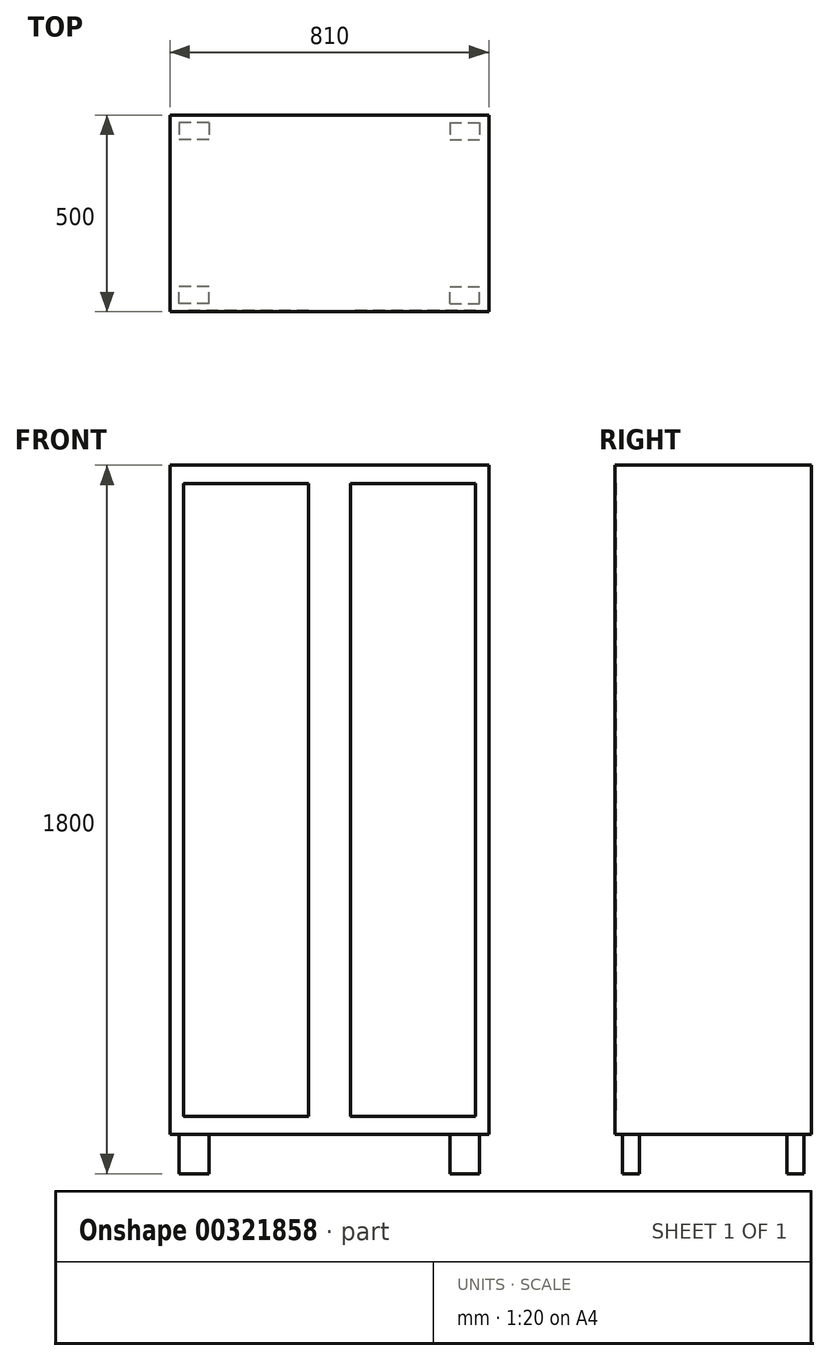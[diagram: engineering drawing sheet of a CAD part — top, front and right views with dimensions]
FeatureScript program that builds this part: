
annotation { "Feature Type Name" : "Feature", "Feature Type Description" : "" }
export const myFeature = defineFeature(function(context is Context, id is Id, definition is map)
    precondition{}
    {
        {
            var Q0;
            Q0=qCreatedBy(makeId("Top.planeOp"),FACE);
            var sketch = newSketch(context, id + "F0", { "sketchPlane" : qUnion([Q0])});
            skLineSegment(sketch, "E0.bottom", {"start": v(405, 250) * mm, "end": v(-405, 250) * mm});
            skLineSegment(sketch, "E0.top", {"start": v(405, -250) * mm, "end": v(-405, -250) * mm});
            skLineSegment(sketch, "E0.left", {"start": v(405, 250) * mm, "end": v(405, -250) * mm});
            skLineSegment(sketch, "E0.right", {"start": v(-405, 250) * mm, "end": v(-405, -250) * mm});
            skPoint(sketch, "E0.middle", {"position": v(0, 0) * mm});
            skSolve(sketch);
        }
        {
            var Q0;
            Q0=makeQuery(id+"F0.imprint","IMPRINT",FACE,{"disambiguationData":[TD([[makeQuery(id+"F0.imprint","IMPRINT",EDGE,{"derivedFrom":sQuery(id+"F0.wireOp",EDGE,"E0.bottom")}),1.0]])]});
            extrude(context, id + "F1", {"entities" : qUnion([Q0]), "depth" : 1700 * mm});
        }
        {
            var Q0;
            Q0=makeQuery(id+"F1.opExtrude","CAP_FACE",FACE,{"disambiguationData":[OSD([sQuery(id+"F0.wireOp",EDGE,"E0.bottom"),sQuery(id+"F0.wireOp",EDGE,"E0.top"),sQuery(id+"F0.wireOp",EDGE,"E0.left"),sQuery(id+"F0.wireOp",EDGE,"E0.right")])],"isStart":true});
            var sketch = newSketch(context, id + "F2", { "sketchPlane" : qUnion([Q0])});
            skLineSegment(sketch, "E1", {"start": v(-405, 0) * mm, "end": v(405, 0) * mm, "construction": true});
            skLineSegment(sketch, "E2", {"start": v(0, -250) * mm, "end": v(0, 250) * mm, "construction": true});
            skLineSegment(sketch, "E3.bottom", {"start": v(-306.12, 229.96) * mm, "end": v(-381.85, 229.96) * mm});
            skLineSegment(sketch, "E3.top", {"start": v(-306.12, 186.8) * mm, "end": v(-381.85, 186.8) * mm});
            skLineSegment(sketch, "E3.left", {"start": v(-306.12, 229.96) * mm, "end": v(-306.12, 186.8) * mm});
            skLineSegment(sketch, "E3.right", {"start": v(-381.85, 229.96) * mm, "end": v(-381.85, 186.8) * mm});
            skPoint(sketch, "E3.middle", {"position": v(-343.99, 208.38) * mm});
            skLineSegment(sketch, "E4.MirrorCS", {"start": v(381.85, 229.96) * mm, "end": v(381.85, 186.8) * mm});
            skLineSegment(sketch, "E5.MirrorCS", {"start": v(306.12, 229.96) * mm, "end": v(381.85, 229.96) * mm});
            skLineSegment(sketch, "E6.MirrorCS", {"start": v(306.12, 229.96) * mm, "end": v(306.12, 186.8) * mm});
            skLineSegment(sketch, "E7.MirrorCS", {"start": v(306.12, 186.8) * mm, "end": v(381.85, 186.8) * mm});
            skLineSegment(sketch, "E8.MirrorCS", {"start": v(381.85, -229.96) * mm, "end": v(381.85, -186.8) * mm});
            skLineSegment(sketch, "E9.MirrorCS", {"start": v(-381.85, -229.96) * mm, "end": v(-381.85, -186.8) * mm});
            skLineSegment(sketch, "E10.MirrorCS", {"start": v(-306.12, -229.96) * mm, "end": v(-306.12, -186.8) * mm});
            skLineSegment(sketch, "E11.MirrorCS", {"start": v(306.12, -229.96) * mm, "end": v(306.12, -186.8) * mm});
            skLineSegment(sketch, "E12.MirrorCS", {"start": v(-306.12, -186.8) * mm, "end": v(-381.85, -186.8) * mm});
            skLineSegment(sketch, "E13.MirrorCS", {"start": v(-306.12, -229.96) * mm, "end": v(-381.85, -229.96) * mm});
            skLineSegment(sketch, "E14.MirrorCS", {"start": v(306.12, -186.8) * mm, "end": v(381.85, -186.8) * mm});
            skLineSegment(sketch, "E15.MirrorCS", {"start": v(306.12, -229.96) * mm, "end": v(381.85, -229.96) * mm});
            skPoint(sketch, "E16.MirrorP", {"position": v(-343.99, -208.38) * mm});
            skSolve(sketch);
        }
        {
            var Q0;
            Q0 = qSketchRegion(id + "F2", true);
            extrude(context, id + "F3", {"entities" : qUnion([Q0]), "operationType" : NewBodyOperationType.ADD, "depth" : 100 * mm});
        }
        {
            var Q0;
            Q0=makeQuery(id+"F1.opExtrude","SWEPT_FACE",FACE,{"disambiguationData":[OSD([sQuery(id+"F0.wireOp",EDGE,"E0.top")])]});
            var sketch = newSketch(context, id + "F4", { "sketchPlane" : qUnion([Q0])});
            skLineSegment(sketch, "E17", {"start": v(0, 0) * mm, "end": v(0, 1700) * mm, "construction": true});
            skLineSegment(sketch, "E18.bottom", {"start": v(-53, 1653.84) * mm, "end": v(-370.83, 1653.84) * mm});
            skLineSegment(sketch, "E18.top", {"start": v(-53, 46.16) * mm, "end": v(-370.83, 46.16) * mm});
            skLineSegment(sketch, "E18.left", {"start": v(-53, 1653.84) * mm, "end": v(-53, 46.16) * mm});
            skLineSegment(sketch, "E18.right", {"start": v(-370.83, 1653.84) * mm, "end": v(-370.83, 46.16) * mm});
            skPoint(sketch, "E18.middle", {"position": v(-211.92, 850) * mm});
            skPoint(sketch, "E18.middle.positionSnap0", {"position": v(-405, 850) * mm});
            skPoint(sketch, "E18.centerSnap0", {"position": v(-405, 850) * mm});
            skPoint(sketch, "E19.MirrorP", {"position": v(405, 850) * mm});
            skLineSegment(sketch, "E20.MirrorCS", {"start": v(370.83, 1653.84) * mm, "end": v(370.83, 46.16) * mm});
            skLineSegment(sketch, "E21.MirrorCS", {"start": v(53, 1653.84) * mm, "end": v(53, 46.16) * mm});
            skLineSegment(sketch, "E22.MirrorCS", {"start": v(53, 1653.84) * mm, "end": v(370.83, 1653.84) * mm});
            skLineSegment(sketch, "E23.MirrorCS", {"start": v(53, 46.16) * mm, "end": v(370.83, 46.16) * mm});
            skPoint(sketch, "E24.MirrorP", {"position": v(211.92, 850) * mm});
            skSolve(sketch);
        }
        {
            var Q0;
            Q0 = qSketchRegion(id + "F4", true);
            extrude(context, id + "F5", {"entities" : qUnion([Q0]), "operationType" : NewBodyOperationType.REMOVE, "oppositeDirection" : true, "depth" : 3 * mm, "hasDraft" : true, "draftAngle" : 10 * degree});
        }
    });
